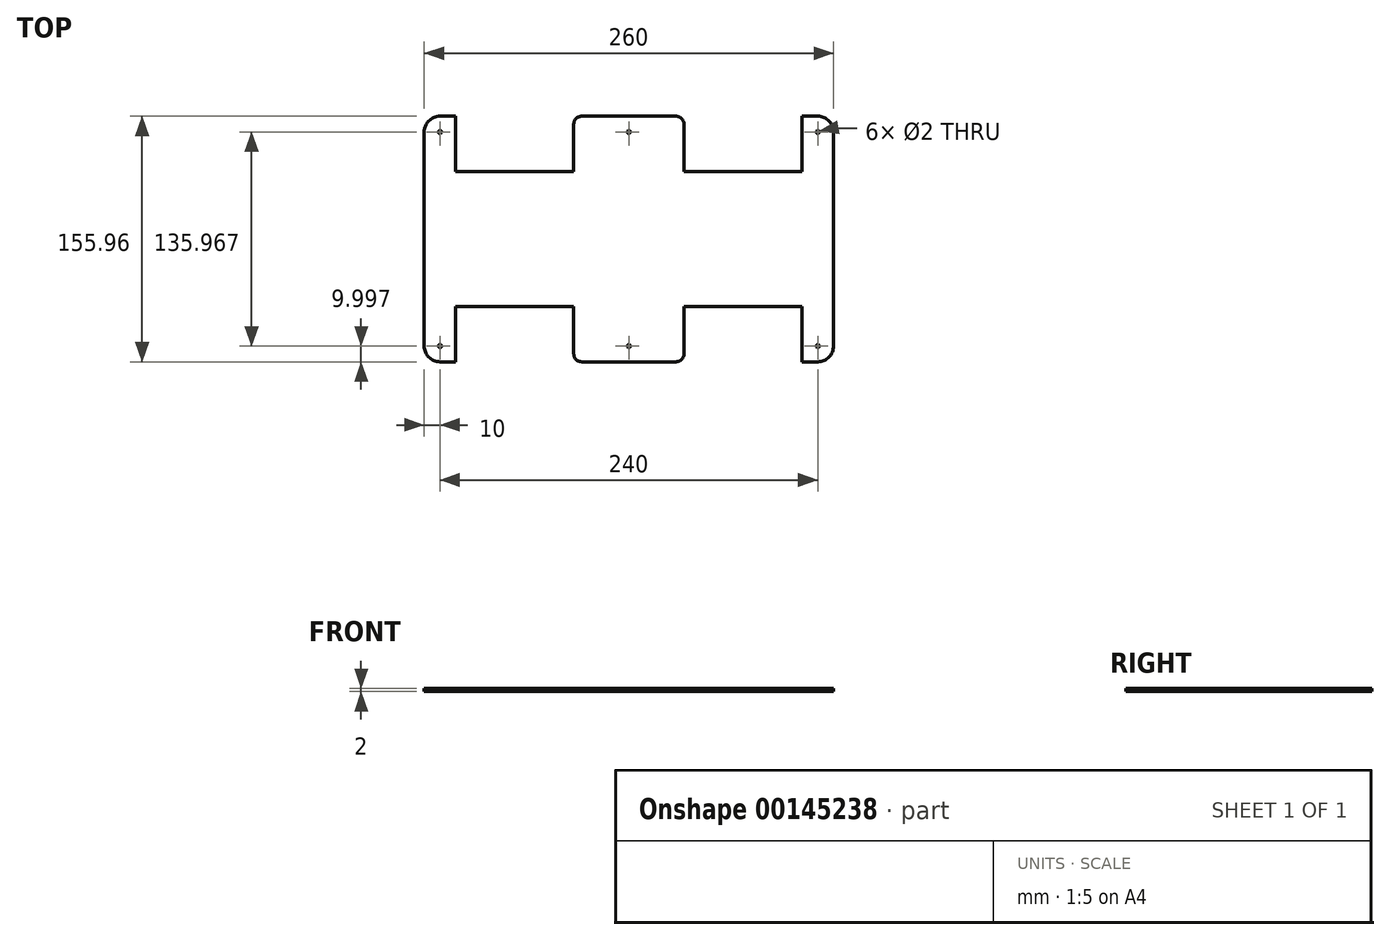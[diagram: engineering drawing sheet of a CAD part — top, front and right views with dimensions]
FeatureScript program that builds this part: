
annotation { "Feature Type Name" : "Feature", "Feature Type Description" : "" }
export const myFeature = defineFeature(function(context is Context, id is Id, definition is map)
    precondition{}
    {
        {
            var Q0;
            Q0=qCreatedBy(makeId("Top.planeOp"),FACE);
            var sketch = newSketch(context, id + "F0", { "sketchPlane" : qUnion([Q0])});
            skLineSegment(sketch, "E0.bottom", {"start": v(120, 77.98) * mm, "end": v(110, 77.98) * mm});
            skLineSegment(sketch, "E0.left", {"start": v(130, 67.98) * mm, "end": v(130, 0) * mm});
            skLineSegment(sketch, "E0.right", {"start": v(-130, 67.98) * mm, "end": v(-130, 0) * mm});
            skPoint(sketch, "E0.middle", {"position": v(0, 0) * mm});
            skLineSegment(sketch, "E1", {"start": v(-110, 77.98) * mm, "end": v(-120, 77.98) * mm});
            skLineSegment(sketch, "E2", {"start": v(30, 77.98) * mm, "end": v(-30, 77.98) * mm});
            skPoint(sketch, "E3.visualSharp", {"position": v(130, 77.98) * mm});
            skArc(sketch, "E3.filletArc", {"start": v(130, 67.98) * mm, "mid": v(127.07, 75.05) * mm, "end": v(120, 77.98) * mm});
            skPoint(sketch, "E4.visualSharp", {"position": v(-130, 77.98) * mm});
            skArc(sketch, "E4.filletArc", {"start": v(-120, 77.98) * mm, "mid": v(-127.07, 75.05) * mm, "end": v(-130, 67.98) * mm});
            skPoint(sketch, "E5.visualSharp", {"position": v(-130, -77.98) * mm});
            skPoint(sketch, "E6.visualSharp", {"position": v(130, -77.98) * mm});
            skLineSegment(sketch, "E7", {"start": v(-110, 77.98) * mm, "end": v(-110, 42.98) * mm});
            skLineSegment(sketch, "E8", {"start": v(-110, 42.98) * mm, "end": v(-35, 42.98) * mm});
            skLineSegment(sketch, "E9", {"start": v(-35, 72.98) * mm, "end": v(-35, 42.98) * mm});
            skLineSegment(sketch, "E10", {"start": v(35, 72.98) * mm, "end": v(35, 42.98) * mm});
            skLineSegment(sketch, "E11", {"start": v(35, 42.98) * mm, "end": v(110, 42.98) * mm});
            skLineSegment(sketch, "E12", {"start": v(110, 42.98) * mm, "end": v(110, 77.98) * mm});
            skPoint(sketch, "E13.visualSharp", {"position": v(-35, 77.98) * mm});
            skArc(sketch, "E13.filletArc", {"start": v(-30, 77.98) * mm, "mid": v(-33.54, 76.52) * mm, "end": v(-35, 72.98) * mm});
            skPoint(sketch, "E14.visualSharp", {"position": v(35, 77.98) * mm});
            skArc(sketch, "E14.filletArc", {"start": v(35, 72.98) * mm, "mid": v(33.54, 76.52) * mm, "end": v(30, 77.98) * mm});
            skLineSegment(sketch, "E15.MirrorCS", {"start": v(-130, -67.98) * mm, "end": v(-130, 0) * mm});
            skArc(sketch, "E16.MirrorCS", {"start": v(-120, -77.98) * mm, "mid": v(-127.07, -75.05) * mm, "end": v(-130, -67.98) * mm});
            skLineSegment(sketch, "E17.MirrorCS", {"start": v(-110, -77.98) * mm, "end": v(-120, -77.98) * mm});
            skLineSegment(sketch, "E18.MirrorCS", {"start": v(-110, -77.98) * mm, "end": v(-110, -42.98) * mm});
            skLineSegment(sketch, "E19.MirrorCS", {"start": v(-110, -42.98) * mm, "end": v(-35, -42.98) * mm});
            skLineSegment(sketch, "E20.MirrorCS", {"start": v(-35, -72.98) * mm, "end": v(-35, -42.98) * mm});
            skArc(sketch, "E21.MirrorCS", {"start": v(-30, -77.98) * mm, "mid": v(-33.54, -76.52) * mm, "end": v(-35, -72.98) * mm});
            skLineSegment(sketch, "E22.MirrorCS", {"start": v(30, -77.98) * mm, "end": v(-30, -77.98) * mm});
            skArc(sketch, "E23.MirrorCS", {"start": v(35, -72.98) * mm, "mid": v(33.54, -76.52) * mm, "end": v(30, -77.98) * mm});
            skLineSegment(sketch, "E24.MirrorCS", {"start": v(35, -72.98) * mm, "end": v(35, -42.98) * mm});
            skLineSegment(sketch, "E25.MirrorCS", {"start": v(35, -42.98) * mm, "end": v(110, -42.98) * mm});
            skLineSegment(sketch, "E26.MirrorCS", {"start": v(110, -42.98) * mm, "end": v(110, -77.98) * mm});
            skLineSegment(sketch, "E27.MirrorCS", {"start": v(120, -77.98) * mm, "end": v(110, -77.98) * mm});
            skArc(sketch, "E28.MirrorCS", {"start": v(130, -67.98) * mm, "mid": v(127.07, -75.05) * mm, "end": v(120, -77.98) * mm});
            skLineSegment(sketch, "E29.MirrorCS", {"start": v(130, -67.98) * mm, "end": v(130, 0) * mm});
            skPoint(sketch, "E30", {"position": v(-130, 0) * mm});
            skPoint(sketch, "E31", {"position": v(130, 0) * mm});
            skCircle(sketch, "E32", {"center": v(-120, 67.98) * mm, "radius": 1 * mm, "construction": true});
            skCircle(sketch, "E33", {"center": v(-120, -67.98) * mm, "radius": 1 * mm});
            skCircle(sketch, "E34", {"center": v(120, 67.98) * mm, "radius": 1 * mm});
            skCircle(sketch, "E35", {"center": v(120, -67.98) * mm, "radius": 1 * mm});
            skLineSegment(sketch, "E36", {"start": v(-120, 67.98) * mm, "end": v(-110, 67.98) * mm});
            skLineSegment(sketch, "E37.trimOffspring", {"start": v(110, 67.98) * mm, "end": v(120, 67.98) * mm});
            skPoint(sketch, "E38.trimOffspring.end.orphan", {"position": v(0, 67.98) * mm});
            skCircle(sketch, "E39", {"center": v(0, 67.98) * mm, "radius": 1 * mm});
            skPoint(sketch, "E40", {"position": v(0, -67.98) * mm});
            skCircle(sketch, "E41", {"center": v(0, -67.98) * mm, "radius": 1 * mm});
            skSolve(sketch);
        }
        {
            var Q0;
            Q0=makeQuery(id+"F0.imprint","IMPRINT",FACE,{"disambiguationData":[TD([[makeQuery(id+"F0.imprint","IMPRINT",EDGE,{"derivedFrom":sQuery(id+"F0.wireOp",EDGE,"E0.bottom")}),1.0]])]});
            extrude(context, id + "F1", {"entities" : qUnion([Q0]), "depth" : 2 * mm});
        }
        {
            var Q0;
            Q0=sQuery(id+"F0.wireOp",VERTEX,"E4.filletArc.center");
            var Q1;
            Q1=makeQuery(id+"F1.opExtrude","SWEPT_BODY",BODY,{"disambiguationData":[OSD([sQuery(id+"F0.wireOp",EDGE,"E0.bottom"),sQuery(id+"F0.wireOp",EDGE,"E0.left"),sQuery(id+"F0.wireOp",EDGE,"E0.right"),sQuery(id+"F0.wireOp",EDGE,"E1"),sQuery(id+"F0.wireOp",EDGE,"E2"),sQuery(id+"F0.wireOp",EDGE,"E3.filletArc"),sQuery(id+"F0.wireOp",EDGE,"E4.filletArc"),sQuery(id+"F0.wireOp",EDGE,"E7"),sQuery(id+"F0.wireOp",EDGE,"E8"),sQuery(id+"F0.wireOp",EDGE,"E9"),sQuery(id+"F0.wireOp",EDGE,"E10"),sQuery(id+"F0.wireOp",EDGE,"E11"),sQuery(id+"F0.wireOp",EDGE,"E12"),sQuery(id+"F0.wireOp",EDGE,"E13.filletArc"),sQuery(id+"F0.wireOp",EDGE,"E14.filletArc"),sQuery(id+"F0.wireOp",EDGE,"E15.MirrorCS"),sQuery(id+"F0.wireOp",EDGE,"E16.MirrorCS"),sQuery(id+"F0.wireOp",EDGE,"E17.MirrorCS"),sQuery(id+"F0.wireOp",EDGE,"E18.MirrorCS"),sQuery(id+"F0.wireOp",EDGE,"E19.MirrorCS"),sQuery(id+"F0.wireOp",EDGE,"E20.MirrorCS"),sQuery(id+"F0.wireOp",EDGE,"E21.MirrorCS"),sQuery(id+"F0.wireOp",EDGE,"E22.MirrorCS"),sQuery(id+"F0.wireOp",EDGE,"E23.MirrorCS"),sQuery(id+"F0.wireOp",EDGE,"E24.MirrorCS"),sQuery(id+"F0.wireOp",EDGE,"E25.MirrorCS"),sQuery(id+"F0.wireOp",EDGE,"E26.MirrorCS"),sQuery(id+"F0.wireOp",EDGE,"E27.MirrorCS"),sQuery(id+"F0.wireOp",EDGE,"E28.MirrorCS"),sQuery(id+"F0.wireOp",EDGE,"E29.MirrorCS"),sQuery(id+"F0.wireOp",EDGE,"E33"),sQuery(id+"F0.wireOp",EDGE,"E34"),sQuery(id+"F0.wireOp",EDGE,"E35")])]});
            hole(context, id + "F2", {"style" : HoleStyle.SIMPLE, "endStyle" : HoleEndStyle.THROUGH, "oppositeDirection" : true, "holeDiameter" : 2 * mm, "locations" : qUnion([Q0]), "scope" : qUnion([Q1]), "isTappedThrough" : true});
        }
    });
